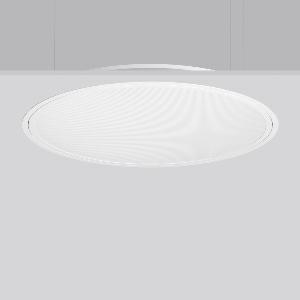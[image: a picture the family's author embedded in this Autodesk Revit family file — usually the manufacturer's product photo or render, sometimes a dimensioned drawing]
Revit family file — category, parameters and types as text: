
# Revit family: triona_round_e_312299_002_1_12_2b4d
name_source: partatom
category: Lighting Fixtures
units: mm (PartAtom-declared; Revit-internal decimal feet)

## family parameters
Cut with Voids When Loaded = No
Host = Face
Light Source = No
Part Type = Normal
Room Calculation Point = No
Round Connector Dimension = Use Diameter
Shared = No

## types (1)
- TRIONA round E (1 x LED Modul 840, 8350 lm, 4000)
    Apparent Load = 66 VA
    CIE Flux Codes = 59 87 97 100 100
    Color Rendering = 80
    Color Temperature = 4000
    Default Elevation = 1800 mm
    Description = Series: TRIONA round
Decorative round LED recessed surface luminaire. Cover made of sheet steel, powder-coated. Frame made of aluminium, powder-coated. Recessed ring: aluminium extrusion profile, powder coated. Light emission through a diffuser in plastic, opal/prismatic. Lightguide and diffuser made of non-yellowing plastic (PMMA). Lateral light emission (RZB SIDELITE technology) for above-average homogeneous light distribution. Suitable for installation in cavity ceilings. Tool-free mounting system thanks to the rocker arm mechanism (patent pending). Electronic ballast included. Very easy installation thanks to Plug+Play connection. 
Colour: traffic white, matt (RAL 9016)
Diameter: 889 mm
Height: 2 mm
Cut-out diameter: 866 mm
Recess height: 100 mm
Luminaire: recess height: 89 mm
Lamp: LED
Socket: without socket
Colour temperature: 4000K
Colour rendering index (CRI): 80
System power: 66 W
Rated luminous flux: 8350 lm
Luminous efficiency: 127 lm/W
Control gear: Converter, dimmable, DALI
Protection class: I
Type of protection: IP 40
    Height = 0 mm  [stored 0 ft]
    Lamp = 1 x LED Modul 840
    Lamp Light Flux = 8350 lm
    Lamp count = 1
    Length = 889 mm
    Lifetime = 50000 h
    Luminous efficacy = 127 lm/W
    Manufacturer = RZB
    ModVariant = No
    Model = 312299.002.1.12
    Mounting Place = Ceiling
    Mounting Type = Recessed
    Number of Poles = 1
    OnlyDefault = Yes
    Power Factor = 1
    Product Name = TRIONA round E
    Product group = Recessed modular luminaires
    ProductGroupID = 406
    Protection Class = Protection class I
    Protection Degree = IP 20
    RLX_Detail_Level = 1
    RLX_Emergency_Light_Flux = 0 lm
    RLX_Emergency_Type = 0
    RLX_Emergency_Type_DB = No
    RlxData = <blob elided: 39445 chars, md5=e8d478e1>
    Socket = socket
    Standby Power = 0 W
    System Light Flux = 8350 lm
    System Power = 66 W
    Type Comments = Product without accessories
    Type Image = 312299.002.12.jpg
    URL = http://relux.com
    VarID = ---
    Voltage = 230 V
    Voltage Range = 220-240 V
    Weight = 0.00 kg
    Width = 0 mm  [stored 0 ft]

note: [stored X ft] marks values corroborated as IEEE doubles in the binary element streams (Revit-internal decimal feet)

## geometry (parser evidence)
native form markers: Blend x4, Sweep x10
no freeform markers — native parametric forms only
